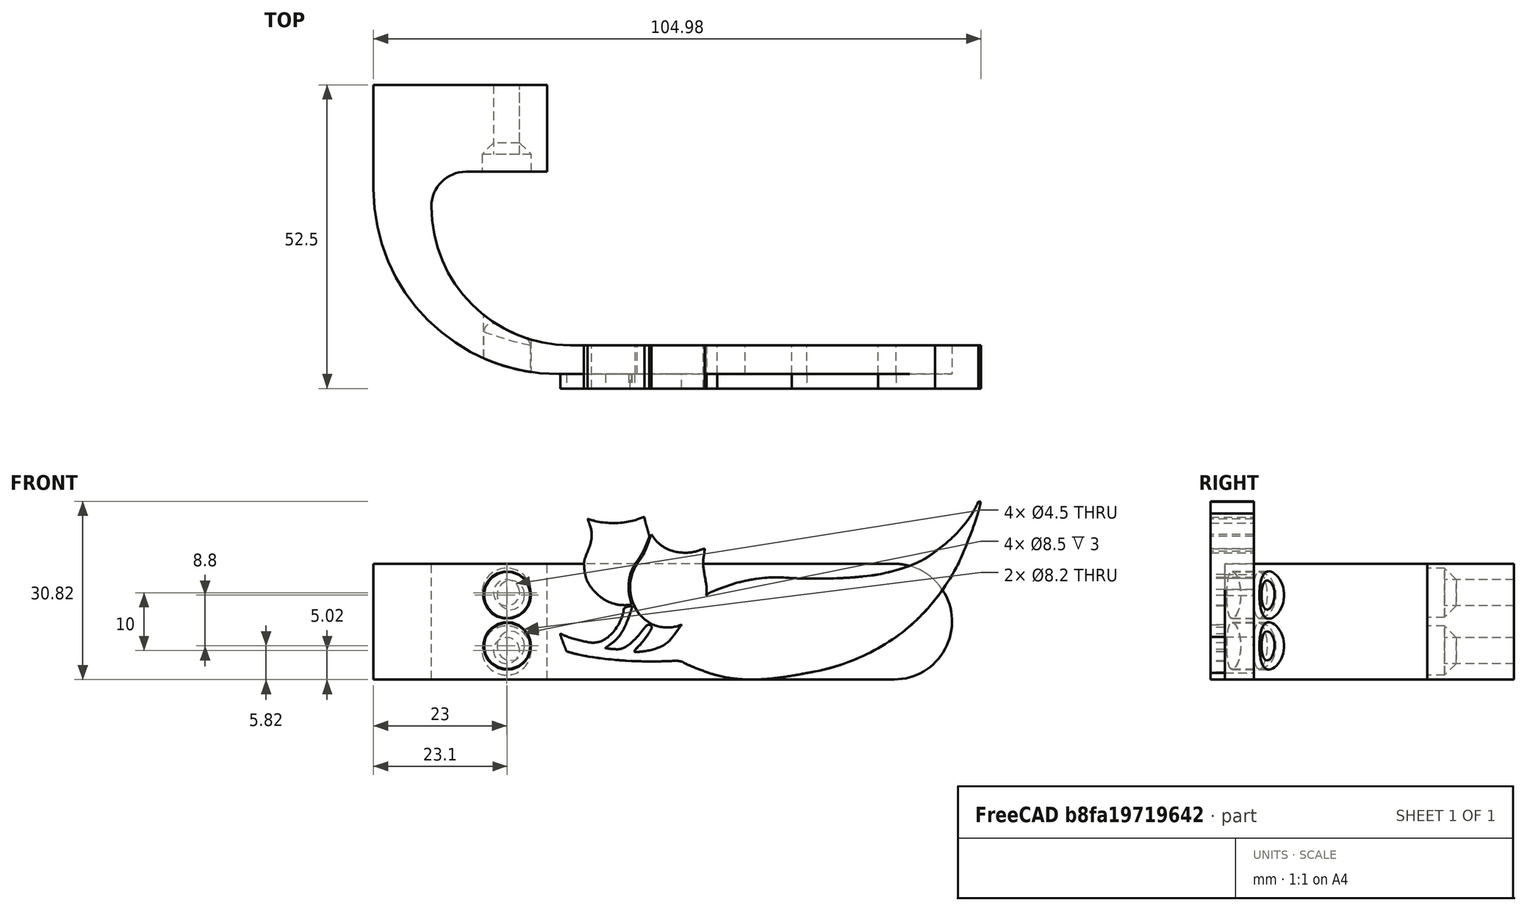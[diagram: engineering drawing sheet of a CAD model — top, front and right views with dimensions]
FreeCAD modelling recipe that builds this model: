
FCSTD DOCUMENT  (FreeCAD 1.0R39109 (Git))
Label: test
License: All rights reserved
LicenseURL: https://en.wikipedia.org/wiki/All_rights_reserved
objects: PartDesign::Pocket×6, Sketcher::SketchObject×5, Part::MultiFuse×5, PartDesign::Pad×4, Part::Feature×4, Part::Cylinder×4, PartDesign::Fillet×3, Part::Extrusion×3, PartDesign::Body×2, PartDesign::Chamfer×1, Part::Scale×1, Part::MultiCommon×1, Part::Fillet×1, Part::Cut×1, PartDesign::FeatureBase×1
note: 76 computed .brp shape members not serialized (recipe doc carries the construction recipe); baked Part::Feature solids carry a one-line shape summary decoded from their .brp

FEATURE [Sketcher::SketchObject] Sketch
  ArcFitTolerance = 1e-06
  AttachmentSupport = -> [XZ_Plane]
  FullyConstrained = true
  MakeInternals = false
  MapMode = 5
  Placement = pos=(0,0,0) rot=(1,0,0;1.5708rad)
  sketch-geometry (4):
    g0: LineSegment StartX=0 StartY=20 StartZ=0 EndX=0 EndY=0 EndZ=0
    g1: LineSegment StartX=0 StartY=0 StartZ=0 EndX=30 EndY=0 EndZ=0
    g2: LineSegment StartX=30 StartY=0 StartZ=0 EndX=30 EndY=20 EndZ=0
    g3: LineSegment StartX=30 StartY=20 StartZ=0 EndX=0 EndY=20 EndZ=0
  constraints (11):
    c: Coincident(g0,g1)
    c: Coincident(g1,g2)
    c: Coincident(g2,g3)
    c: Coincident(g3,g0)
    c: Vertical(g0)
    c: Vertical(g2)
    c: Horizontal(g1)
    c: Horizontal(g3)
    c: Distance(g0,g2) = 30
    c: Distance(g1,g3) = 20
    c: Coincident(g0,g-1)
FEATURE [PartDesign::Pad] Pad
  Direction = (0,-1,2e-16)
  Length = 15
  Length2 = 10
  Placement = pos=(0,0,0) rot=(1,0,0;1.5708rad)
  Profile = -> Sketch
  ReferenceAxis = -> Sketch [N_Axis]
  Refine = true
  Suppressed = false
  Type = 0
FEATURE [Sketcher::SketchObject] Sketch001
  ArcFitTolerance = 1e-06
  AttachmentSupport = -> [Pad]
  ExternalGeometry = -> [Pad]
  FullyConstrained = true
  MakeInternals = false
  MapMode = 5
  Placement = pos=(0,-15,0) rot=(1,0,0;1.5708rad)
  sketch-geometry (4):
    g0: Circle CenterX=23 CenterY=15 CenterZ=0 NormalX=0 NormalY=0 NormalZ=1 AngleXU=0 Radius=2.25
    g1: Circle CenterX=23 CenterY=5 CenterZ=0 NormalX=0 NormalY=0 NormalZ=1 AngleXU=0 Radius=2.25
    g2: Circle CenterX=23 CenterY=15 CenterZ=0 NormalX=0 NormalY=0 NormalZ=1 AngleXU=0 Radius=4.25
    g3: Circle CenterX=23 CenterY=5 CenterZ=0 NormalX=0 NormalY=0 NormalZ=1 AngleXU=0 Radius=4.25
  constraints (10):
    c: Diameter(g0) = 4.5
    c: Diameter(g1) = 4.5
    c: Distance(g0,g-3) = 7
    c: Vertical(g1,g0)
    c: DistanceY(g-1,g1) = 5
    c: Distance(g0,g-4) = 5
    c: Diameter(g2) = 8.5
    c: Coincident(g2,g0)
    c: Diameter(g3) = 8.5
    c: Coincident(g3,g1)
FEATURE [Sketcher::SketchObject] Sketch002
  ArcFitTolerance = 1e-06
  AttachmentSupport = -> [Pad]
  ExternalGeometry = -> [Pad]
  FullyConstrained = true
  MakeInternals = false
  MapMode = 5
  Placement = pos=(0,-15,0) rot=(1,0,0;1.5708rad)
  sketch-geometry (4):
    g0: LineSegment StartX=0 StartY=0 StartZ=0 EndX=10 EndY=0 EndZ=0
    g1: LineSegment StartX=10 StartY=0 StartZ=0 EndX=10 EndY=20 EndZ=0
    g2: LineSegment StartX=10 StartY=20 StartZ=0 EndX=0 EndY=20 EndZ=0
    g3: LineSegment StartX=0 StartY=20 StartZ=0 EndX=0 EndY=0 EndZ=0
  constraints (11):
    c: Coincident(g0,g1)
    c: Coincident(g1,g2)
    c: Coincident(g2,g3)
    c: Coincident(g3,g0)
    c: Horizontal(g0)
    c: Horizontal(g2)
    c: Vertical(g1)
    c: Vertical(g3)
    c: Distance(g1,g3) = 10
    c: Coincident(g0,g-1)
    c: PointOnObject(g1,g-3)
FEATURE [PartDesign::Pad] Pad001
  BaseFeature = -> Pad
  Direction = (0,-1,2e-16)
  Length = 35
  Length2 = 10
  Placement = pos=(0,0,0) rot=(1,0,0;1.5708rad)
  Profile = -> Sketch002
  ReferenceAxis = -> Sketch002 [N_Axis]
  Refine = true
  Suppressed = false
  Type = 0
FEATURE [Sketcher::SketchObject] Sketch003
  ArcFitTolerance = 1e-06
  AttachmentSupport = -> [Pad001]
  ExternalGeometry = -> [Pad001]
  FullyConstrained = true
  MakeInternals = false
  MapMode = 5
  Placement = pos=(10,0,0) rot=(0.707107,0,0.707107;3.14159rad)
  sketch-geometry (4):
    g0: LineSegment StartX=0 StartY=50 StartZ=0 EndX=0 EndY=45 EndZ=0
    g1: LineSegment StartX=0 StartY=45 StartZ=0 EndX=20 EndY=45 EndZ=0
    g2: LineSegment StartX=20 StartY=45 StartZ=0 EndX=20 EndY=50 EndZ=0
    g3: LineSegment StartX=20 StartY=50 StartZ=0 EndX=0 EndY=50 EndZ=0
  constraints (11):
    c: Coincident(g0,g1)
    c: Coincident(g1,g2)
    c: Coincident(g2,g3)
    c: Coincident(g3,g0)
    c: Vertical(g0)
    c: Vertical(g2)
    c: Horizontal(g1)
    c: Horizontal(g3)
    c: Distance(g1,g3) = 5
    c: Coincident(g0,g-3)
    c: PointOnObject(g1,g-4)
FEATURE [PartDesign::Pad] Pad002
  BaseFeature = -> Pad001
  Direction = (1,0,-2e-16)
  Length = 80
  Length2 = 10
  Placement = pos=(0,0,0) rot=(1,0,0;1.5708rad)
  Profile = -> Sketch003
  ReferenceAxis = -> Sketch003 [N_Axis]
  Refine = true
  Suppressed = false
  Type = 0
FEATURE [PartDesign::Fillet] Fillet
  Base = -> Pad002 [Edge11]
  BaseFeature = -> Pad002
  Placement = pos=(0,0,0) rot=(1,0,0;1.5708rad)
  Radius = 6
  Refine = true
  SupportTransform = false
  Suppressed = false
  UseAllEdges = false
FEATURE [PartDesign::Fillet] Fillet001
  Base = -> Fillet [Edge23]
  BaseFeature = -> Fillet
  Placement = pos=(0,0,0) rot=(1,0,0;1.5708rad)
  Radius = 23.99
  Refine = true
  SupportTransform = false
  Suppressed = false
  UseAllEdges = false
FEATURE [PartDesign::Fillet] Fillet002
  Base = -> Fillet001 [Edge27]
  BaseFeature = -> Fillet001
  Placement = pos=(0,0,0) rot=(1,0,0;1.5708rad)
  Radius = 32
  Refine = true
  SupportTransform = false
  Suppressed = false
  UseAllEdges = false
FEATURE [Sketcher::SketchObject] Sketch004
  ArcFitTolerance = 1e-06
  AttachmentSupport = -> [Fillet002]
  ExternalGeometry = -> [Fillet002]
  FullyConstrained = true
  MakeInternals = false
  MapMode = 5
  Placement = pos=(0,-50,1.8e-14) rot=(1,0,0;1.5708rad)
  sketch-geometry (2):
    g0: ArcOfCircle CenterX=90 CenterY=10 CenterZ=0 NormalX=0 NormalY=0 NormalZ=1 AngleXU=0 Radius=10 StartAngle=4.71239 EndAngle=7.85398
    g1: LineSegment StartX=90 StartY=20 StartZ=0 EndX=90 EndY=-2.49e-14 EndZ=0
  constraints (5):
    c: Symmetric(g-3,g-3,g0)
    c: Coincident(g0,g-3)
    c: Coincident(g1,g0)
    c: Coincident(g1,g0)
    c: Vertical(g1)
FEATURE [PartDesign::Pad] Pad003
  BaseFeature = -> Fillet002
  Direction = (0,-1,2e-16)
  Length = 5
  Length2 = 10
  Placement = pos=(0,0,0) rot=(1,0,0;1.5708rad)
  Profile = -> Sketch004
  ReferenceAxis = -> Sketch004 [N_Axis]
  Refine = true
  Reversed = true
  Suppressed = false
  Type = 0
FEATURE [PartDesign::Pocket] Pocket
  BaseFeature = -> Pad003
  Direction = (0,1,-2e-16)
  Length = 5
  Length2 = 5
  Placement = pos=(0,0,0) rot=(1,0,0;1.5708rad)
  Profile = -> Sketch001 [Edge1,Edge2]
  ReferenceAxis = -> Sketch001 [N_Axis]
  Refine = true
  Suppressed = false
  Type = 1
FEATURE [PartDesign::Pocket] Pocket001
  BaseFeature = -> Pocket
  Direction = (0,1,-2e-16)
  Length = 3
  Length2 = 5
  Placement = pos=(0,0,0) rot=(1,0,0;1.5708rad)
  Profile = -> Sketch001 [Edge3,Edge4]
  ReferenceAxis = -> Sketch001 [N_Axis]
  Refine = true
  Suppressed = false
  Type = 0
FEATURE [PartDesign::Body] Body
  AllowCompound = false
  Group = -> [Sketch,Pad,Sketch001,Sketch002,Pad001,Sketch003,Pad002,Fillet,Fillet001,Fillet002,Sketch004,Pad003,Pocket,Pocket001]
  Origin = -> Origin
  Tip = -> Pocket001
FEATURE [PartDesign::Chamfer] Chamfer
  Angle = 45
  Base = -> Pocket001 [Edge40,Edge38]
  BaseFeature = -> Pocket001
  ChamferType = 0
  FlipDirection = false
  Placement = pos=(0,0,0) rot=(1,0,0;1.5708rad)
  Refine = true
  Size = 1.99
  Size2 = 1
  SupportTransform = false
  Suppressed = false
  UseAllEdges = false
FEATURE [Part::Feature] path5269
  shape: bbox 102.4 x 120.2 x 2e-07 mm, 0 faces, 0 solids (baked)
FEATURE [Part::Feature] path5271
  shape: bbox 31.93 x 28.89 x 2e-07 mm, 0 faces, 0 solids (baked)
FEATURE [Part::Feature] path5273
  shape: bbox 32.05 x 24.66 x 2e-07 mm, 0 faces, 0 solids (baked)
FEATURE [Part::Extrusion] Extrude
  Base = -> path5269
  Dir = (0,0,-1)
  DirMode = 2
  FaceMakerClass = Part::FaceMakerBullseye
  FaceMakerMode = 3
  LengthFwd = 15
  LengthRev = 0
  Solid = true
  Symmetric = false
FEATURE [Part::Extrusion] Extrude001
  Base = -> path5271
  Dir = (0,0,-1)
  DirMode = 2
  FaceMakerClass = Part::FaceMakerBullseye
  FaceMakerMode = 3
  LengthFwd = 15
  LengthRev = 0
  Solid = true
  Symmetric = false
FEATURE [Part::Extrusion] Extrude003
  Base = -> path5273
  Dir = (0,0,-1)
  DirMode = 2
  FaceMakerClass = Part::FaceMakerBullseye
  FaceMakerMode = 3
  LengthFwd = 15
  LengthRev = 0
  Solid = true
  Symmetric = false
FEATURE [Part::MultiFuse] Fusion
  Shapes = -> [Extrude,Extrude001,Extrude003]
FEATURE [Part::Scale] Scale
  Base = -> Fusion
  Placement = pos=(81.4497,-52.6,61.4516) rot=(-0.717088,-0.492841,0.492841;4.3858rad)
  Uniform = true
  UniformScale = 0.5
  XScale = 1
  YScale = 1
  ZScale = 1
FEATURE [Part::Cylinder] Cylinder
  Angle = 360
  AttacherType = Attacher::AttachEngine3D
  FirstAngle = 0
  Height = 50
  Placement = pos=(22.3,1.3e-15,5.8) rot=(1,0,0;1.5708rad)
  Radius = 4
  SecondAngle = 0
FEATURE [Part::Cylinder] Cylinder001
  Angle = 360
  AttacherType = Attacher::AttachEngine3D
  FirstAngle = 0
  Height = 50
  Placement = pos=(22.3,3.3e-15,14.6) rot=(1,0,0;1.5708rad)
  Radius = 4
  SecondAngle = 0
FEATURE [Part::MultiFuse] Fusion001
  Placement = pos=(0.8,-16.2,0) rot=(0,0,1;0rad)
  Shapes = -> [Cylinder,Cylinder001]
FEATURE [Part::MultiFuse] Fusion002
  Placement = pos=(127.1,-97.6,-5.4) rot=(0,0,1;3.14159rad)
  Shapes = -> [Scale]
FEATURE [Part::Feature] Chamfer001
  Placement = pos=(0,0,0) rot=(1,0,0;1.5708rad)
  shape: bbox 100 x 50 x 20 mm, 21 faces (baked)
FEATURE [Part::MultiCommon] Common
  Shapes = -> [Fusion001,Chamfer001]
FEATURE [Part::Fillet] Fillet003
  Base = -> Common
  EdgeLinks = -> Common [Edge1,Edge4]
  Edges = 2 edges r=1.49: [Edge1,Edge4]
FEATURE [Part::Cylinder] Cylinder002
  Angle = 360
  AttacherType = Attacher::AttachEngine3D
  FirstAngle = 0
  Height = 50
  Placement = pos=(22.3,1.3e-15,5.8) rot=(1,0,0;1.5708rad)
  Radius = 4.1
  SecondAngle = 0
FEATURE [Part::Cylinder] Cylinder003
  Angle = 360
  AttacherType = Attacher::AttachEngine3D
  FirstAngle = 0
  Height = 50
  Placement = pos=(22.3,0,14.6) rot=(1,0,0;1.5708rad)
  Radius = 4.1
  SecondAngle = 0
FEATURE [Part::MultiFuse] Fusion003
  Placement = pos=(0.8,-16.2,0) rot=(0,0,1;0rad)
  Shapes = -> [Cylinder002,Cylinder003]
FEATURE [Part::Cut] Cut
  Base = -> Chamfer
  Tool = -> Fusion003
FEATURE [Part::MultiFuse] Fusion004
  Shapes = -> [Fusion002,Cut]
FEATURE [PartDesign::FeatureBase] BaseFeature
  BaseFeature = -> Fusion004
  Suppressed = false
FEATURE [PartDesign::Pocket] Pocket002
  BaseFeature = -> BaseFeature
  Direction = (0,1,0)
  Length = 5
  Length2 = 5
  Profile = -> BaseFeature [Face45]
  Refine = true
  Suppressed = false
  Type = 0
FEATURE [PartDesign::Pocket] Pocket003
  BaseFeature = -> Pocket002
  Direction = (0,1,0)
  Length = 5
  Length2 = 5
  Profile = -> Pocket002 [Face38]
  Refine = true
  Suppressed = false
  Type = 0
FEATURE [PartDesign::Pocket] Pocket004
  BaseFeature = -> Pocket003
  Direction = (-1.42685,0,0.244826)
  Length = 5
  Length2 = 5
  Profile = -> Pocket003 [Face7]
  Refine = true
  Suppressed = false
  Type = 0
FEATURE [PartDesign::Pocket] Pocket005
  BaseFeature = -> Pocket004
  Direction = (3e-16,1,0)
  Length = 5
  Length2 = 5
  Profile = -> Pocket004 [Face5,Face78,Face77]
  Refine = true
  Suppressed = false
  Type = 0
FEATURE [PartDesign::Body] Body001
  AllowCompound = false
  BaseFeature = -> Fusion004
  Group = -> [BaseFeature,Pocket002,Pocket003,Pocket004,Pocket005]
  Origin = -> Origin001
  Tip = -> Pocket005
